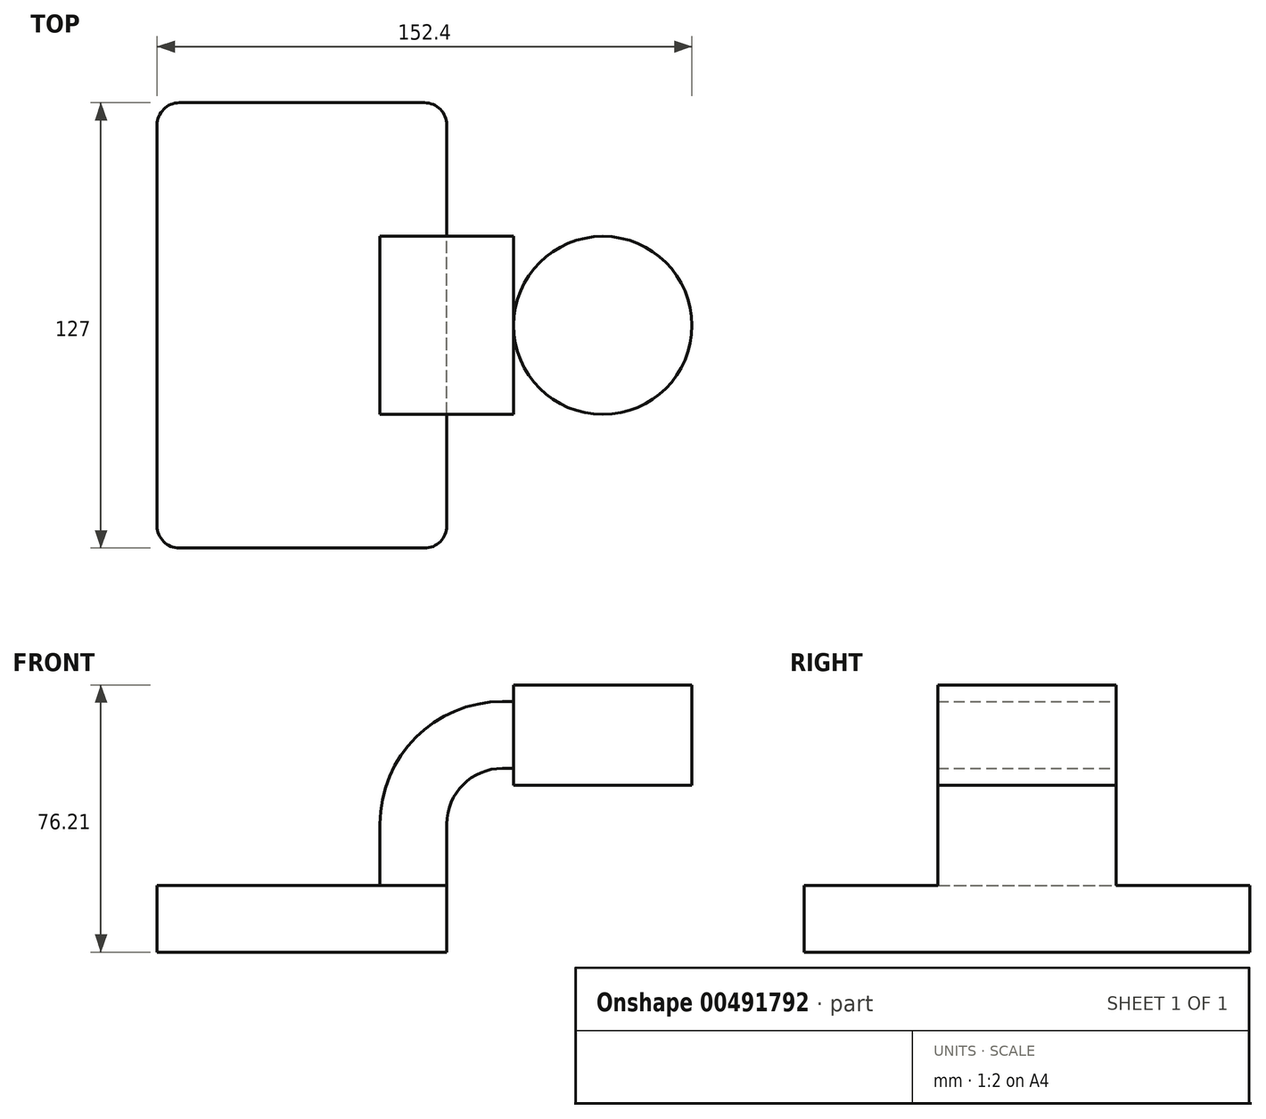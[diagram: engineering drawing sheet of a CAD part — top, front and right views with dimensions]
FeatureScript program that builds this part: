
annotation { "Feature Type Name" : "Feature", "Feature Type Description" : "" }
export const myFeature = defineFeature(function(context is Context, id is Id, definition is map)
    precondition{}
    {
        {
            var Q0;
            Q0=qCreatedBy(makeId("Front.planeOp"),FACE);
            var sketch = newSketch(context, id + "F0", { "sketchPlane" : qUnion([Q0])});
            skLineSegment(sketch, "E0.bottom", {"start": v(-41.28, -9.52) * mm, "end": v(41.28, -9.52) * mm});
            skLineSegment(sketch, "E0.top", {"start": v(-41.28, 9.53) * mm, "end": v(41.28, 9.53) * mm});
            skLineSegment(sketch, "E0.left", {"start": v(-41.27, -9.52) * mm, "end": v(-41.28, 9.53) * mm});
            skLineSegment(sketch, "E0.right", {"start": v(41.28, -9.52) * mm, "end": v(41.28, 9.53) * mm});
            skPoint(sketch, "E0.middle", {"position": v(0, 0) * mm});
            skLineSegment(sketch, "E1.bottom", {"start": v(60.32, 66.68) * mm, "end": v(111.12, 66.68) * mm});
            skLineSegment(sketch, "E1.top", {"start": v(60.33, 38.1) * mm, "end": v(111.12, 38.1) * mm});
            skLineSegment(sketch, "E1.left", {"start": v(60.32, 66.67) * mm, "end": v(60.33, 38.1) * mm});
            skLineSegment(sketch, "E1.right", {"start": v(111.12, 66.67) * mm, "end": v(111.12, 38.1) * mm});
            skPoint(sketch, "E1.middle", {"position": v(85.72, 52.39) * mm});
            skLineSegment(sketch, "E2", {"start": v(41.27, 9.53) * mm, "end": v(41.27, 27) * mm});
            skArc(sketch, "E3", {"start": v(41.27, 27) * mm, "mid": v(45.92, 38.23) * mm, "end": v(57.15, 42.88) * mm});
            skLineSegment(sketch, "E4", {"start": v(57.15, 42.88) * mm, "end": v(85.72, 42.88) * mm});
            skLineSegment(sketch, "E5.0", {"start": v(57.15, 61.93) * mm, "end": v(85.72, 61.93) * mm});
            skArc(sketch, "E5.1", {"start": v(22.22, 27) * mm, "mid": v(32.45, 51.7) * mm, "end": v(57.15, 61.93) * mm});
            skLineSegment(sketch, "E5.2", {"start": v(22.22, 9.53) * mm, "end": v(22.22, 27) * mm});
            skFitSpline(sketch, "E6", {"points": [v(-41.28, 9.53) * mm, v(57.15, 61.93) * mm], "startDerivative": vector(1.98, 115.43) * mm, "endDerivative": vector(149.09, -1.13) * mm});
            skLineSegment(sketch, "E7", {"start": v(85.72, 42.88) * mm, "end": v(85.72, 61.93) * mm});
            skLineSegment(sketch, "E8", {"start": v(85.72, 38.1) * mm, "end": v(85.72, 66.68) * mm});
            skSolve(sketch);
        }
        {
            var Q0;
            Q0=makeQuery(id+"F0.imprint","IMPRINT",FACE,{"disambiguationData":[TD([[makeQuery(id+"F0.imprint","IMPRINT",EDGE,{"derivedFrom":sQuery(id+"F0.wireOp",EDGE,"E0.bottom")}),1.0]])]});
            extrude(context, id + "F1", {"entities" : qUnion([Q0]), "endBound" : BoundingType.SYMMETRIC, "depth" : 127 * mm});
        }
        {
            var Q0;
            {var subQ1=sQuery(id+"F0.wireOp",EDGE,"E2");Q0=makeQuery(id+"F0.imprint","IMPRINT",FACE,{"disambiguationData":[TD([[makeQuery(id+"F0.imprint","IMPRINT",EDGE,{"derivedFrom":subQ1}),1.0]])]});}
            extrude(context, id + "F2", {"entities" : qUnion([Q0]), "operationType" : NewBodyOperationType.ADD, "endBound" : BoundingType.SYMMETRIC, "depth" : 50.8 * mm});
        }
        {
            var Q0;
            Q0=makeQuery(id+"F0.imprint","IMPRINT",FACE,{"disambiguationData":[TD([[makeQuery(id+"F0.imprint","IMPRINT",EDGE,{"derivedFrom":sQuery(id+"F0.wireOp",EDGE,"E5.1")}),1.0]])]});
            extrude(context, id + "F3", {"entities" : qUnion([Q0]), "operationType" : NewBodyOperationType.ADD, "endBound" : BoundingType.SYMMETRIC, "depth" : 15.88 * mm});
        }
        {
            var Q0;
            {var subQ4=sQuery(id+"F0.wireOp",EDGE,"E1.right");Q0=makeQuery(id+"F0.imprint","IMPRINT",FACE,{"disambiguationData":[TD([[makeQuery(id+"F0.imprint","IMPRINT",EDGE,{"derivedFrom":subQ4}),-1.0]])]});}
            var Q1;
            Q1=sQuery(id+"F0.wireOp",EDGE,"E8");
            revolve(context, id + "F4", {"entities" : qUnion([Q0]), "axis" : qUnion([Q1]), "revolveType" : RevolveType.FULL});
        }
        {
            var Q0;
            Q0=makeQuery(id+"F1.opExtrude","CAP_EDGE",EDGE,{"disambiguationData":[OSD([sQuery(id+"F0.wireOp",EDGE,"E0.right")])],"isStart":false});
            var Q1;
            Q1=makeQuery(id+"F1.opExtrude","CAP_EDGE",EDGE,{"disambiguationData":[OSD([sQuery(id+"F0.wireOp",EDGE,"E0.left")])],"isStart":false});
            var Q2;
            Q2=makeQuery(id+"F1.opExtrude","CAP_EDGE",EDGE,{"disambiguationData":[OSD([sQuery(id+"F0.wireOp",EDGE,"E0.right")])],"isStart":true});
            var Q3;
            Q3=makeQuery(id+"F1.opExtrude","CAP_EDGE",EDGE,{"disambiguationData":[OSD([sQuery(id+"F0.wireOp",EDGE,"E0.left")])],"isStart":true});
            fillet(context, id + "F5", {"entities" : qUnion([Q0, Q1, Q2, Q3]), "radius" : 6.35 * mm, "tangentPropagation" : true, "allowEdgeOverflow" : false});
        }
    });
